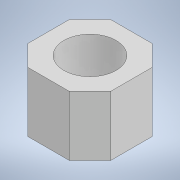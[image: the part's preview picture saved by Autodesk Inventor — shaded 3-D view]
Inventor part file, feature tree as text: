
AUTODESK INVENTOR PART (.ipt)
format: ipt  version: 2020 (Build 240168000, 168)  size: 101,376 bytes
history: native  units: in
note: dims shown in document units (in); Inventor stores cm internally (conversion verified against a paired STEP export)
features: extrude x1, sketch x1
ambient origin geometry x8: Origin, YZ Plane, XZ Plane, XY Plane, X Axis, Y Axis, Z Axis, Center Point
bodies: Solid1 (feature_tree)
feature tree (2):
  extrude  "Extrusion1"  Depth=1.3287in
  sketch  "Sketch1"  dims[d0=1.3287in d1=1.3287in d2=0.8362in d3=0.9606in d4=0.0in]
